# Revit family: Reece_Vanity_Kado_Lussi
name_source: partatom
category: Casework
revit_build: Autodesk Revit 2018 (Build: 20190510_1515(x64)
units: mm (PartAtom-declared; Revit-internal decimal feet)

## family parameters
Always vertical = Yes
Cut with Voids When Loaded = Yes
Room Calculation Point = Yes
Shared = Yes
Work Plane-Based = Yes

## types (1)
- Reece_All_Types
    Default Elevation = 0 mm  [stored 0 ft]
    Description = -
    Disclaimer = THIS FILE IS THE PROPERTY OF THE REECE GROUP. IT MAY NOT BE REPRODUCED, REVERSE-ENGINEERED OR MODIFIED. ANY REPUBLICATION, TRANSMISSION OR DISTRIBUTION FOR THE PURPOSE OF COMMERCIALLY EXPLOITING THE FILES IS PROHIBITED.
    Finish = Please refer to Colour, Finish and Material Variations Document for more information.
    Keynote = Product #, Reece_Vanity_Kado_Lussi - Reece_All_Types
    Manufacturer = Kado
    Model = Lussi
    Reece_Cabinet_Divider = Yes
    Reece_Countertop_Thickness = 80 mm
    Reece_Detail_Additional = Basin included
    Reece_Detail_Bowl Type = Double Bowl
    Reece_Detail_Disclaimer = THIS FILE IS THE PROPERTY OF THE REECE GROUP. IT MAY NOT BE REPRODUCED, REVERSE-ENGINEERED OR MODIFIED. ANY REPUBLICATION, TRANSMISSION OR DISTRIBUTION FOR THE PURPOSE OF COMMERCIALLY EXPLOITING THE FILES IS PROHIBITED.
    Reece_Detail_Taphole Configuration = 0 or 2 Tapholes
0 or 2 Tapholes
0 or 2 Tapholes
    Reece_Door = No
    Reece_Drawer = Yes
    Reece_Material_Cabinet = Reece_Oak_Prime
    Reece_Material_Main = Reece_Solid_Surface_Matte_White
    Reece_Material_Secondary = Reece_Linen_Grey
    Reece_Mid_Door = No
    Reece_Mid_Door_Offset = 501 mm
    Reece_Overall_Depth = 480 mm  [stored 1.5748 ft]
    Reece_Overall_Height = 400 mm
    Reece_Overall_Width = 1500 mm  [stored 4.92126 ft]
    Reece_Product_Brand = Kado
    Reece_Product_Finishes_Web Page = https://digitalassets.reecegroup.com.au
    Reece_Product_Mount = Wall Mounted
    Reece_Product_Sub Brand = Lussi
    Reece_Product_Type = Vanity
    Reece_Rear_Shelf_Basin_Offset = 100 mm  [stored 0.328084 ft]
    Reece_Side_Shelf_Basin_RH_Offset = 103 mm
    Reece_Vanity_Double_Bowl = Yes
    Reece_Vanity_With_Doors = No
    Reece_Vanity_With_Drawers = Yes
    Type Comments = Vanity
    URL = -

note: [stored X ft] marks values corroborated as IEEE doubles in the binary element streams (Revit-internal decimal feet)

## geometry (parser evidence)
native form markers: Sweep x9
no freeform markers — native parametric forms only
